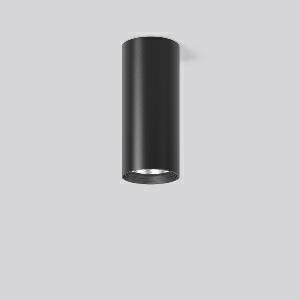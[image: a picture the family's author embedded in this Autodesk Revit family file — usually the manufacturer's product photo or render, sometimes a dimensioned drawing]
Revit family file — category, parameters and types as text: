
# Revit family: heledon_mini_a_931209_003_2_76_ddac
name_source: partatom
category: Lighting Fixtures
units: mm (PartAtom-declared; Revit-internal decimal feet)

## family parameters
Cut with Voids When Loaded = No
Host = Face
Light Source = No
Part Type = Normal
Room Calculation Point = No
Round Connector Dimension = Use Diameter
Shared = No

## types (1)
- HELEDON mini A (1 x LED Modul 927, 3300 lm, 2700)
    Apparent Load = 29 VA
    Approval mark = CE
    CIE Flux Codes = 99 100 100 100 100
    Color Rendering = 92
    Color Temperature = 2700
    Default Elevation = 1800 mm
    Description = Series: HELEDON mini
Cylindrical surface-mounted downlight. Housing: die-cast aluminium, powder-coated. Internal ceiling frame polycarbonate with bayonet mounting. Black plastic ring and recessed LED to prevent glare from the side. Optical assembly with reflector made of MIRO-Silver with 98% total light reflection for outstanding efficiency - can be changed without tools. Best colour rendering index Ra>90. Suitable for Ceiling mounting. Easy installation with a separate ceiling frame with bayonet mounting and plug connection. Driver integrated. Connected via plug-in connector. High quality converter without flickering and stroboscopic effect. The following accessories can be mounted without use of tools: interchangeable lenses, decorative glasses, honeycomb louvre, clear and frosted diffusers, white interchangeable plastic ring. 
Colour: deep black, matt (RAL 9005)
Diameter: 87 mm
Height: 197 mm
Lamp: LED
Socket: without socket
Colour temperature: 2700K
Colour rendering index (CRI): 92
System power: 29 W
Rated luminous flux: 3300 lm
Luminous efficiency: 114 lm/W
Control gear: Converter, dimmable, DALI
Protection class: I
Type of protection: IP 20
    Height = 197 mm
    Lamp = 1 x LED Modul 927
    Lamp Light Flux = 3300 lm
    Lamp count = 1
    Length = 87 mm
    Lifetime = 50000 h
    Luminous efficacy = 114 lm/W
    Manufacturer = RZB
    ModVariant = No
    Model = 931209.003.2.76
    Mounting Place = Ceiling
    Mounting Type = Surface mounted
    Number of Poles = 1
    OnlyDefault = Yes
    Power Factor = 1
    Product Name = HELEDON mini A
    Product group = Surface mounted downlights
    ProductGroupID = 302
    Protection Class = Protection class I
    Protection Degree = IP 20
    RLX_Detail_Level = 1
    RLX_Emergency_Light_Flux = 0 lm
    RLX_Emergency_Type = 0
    RLX_Emergency_Type_DB = No
    RlxData = <blob elided: 108289 chars, md5=bd4abf88>
    Socket = socket
    Standby Power = 0 W
    System Light Flux = 3300 lm
    System Power = 29 W
    Type Comments = Product without accessories
    Type Image = 931188.003.jpg
    URL = http://relux.com
    VarID = ---
    Voltage = 230 V
    Voltage Range = 220-240 V
    Weight = 0.00 kg
    Width = 0 mm  [stored 0 ft]

note: [stored X ft] marks values corroborated as IEEE doubles in the binary element streams (Revit-internal decimal feet)

## geometry (parser evidence)
native form markers: Blend x4, Sweep x8
no freeform markers — native parametric forms only
